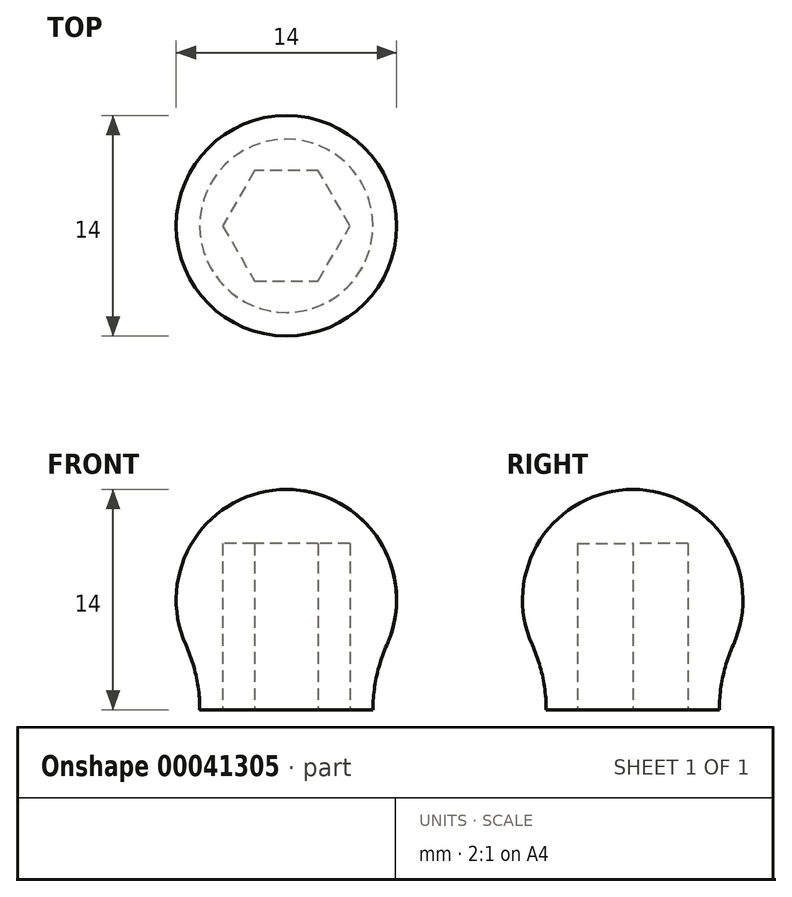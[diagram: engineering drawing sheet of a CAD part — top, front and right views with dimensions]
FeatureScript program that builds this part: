
annotation { "Feature Type Name" : "Feature", "Feature Type Description" : "" }
export const myFeature = defineFeature(function(context is Context, id is Id, definition is map)
    precondition{}
    {
        {
            var Q0;
            Q0=qCreatedBy(makeId("Front.planeOp"),FACE);
            var sketch = newSketch(context, id + "F0", { "sketchPlane" : qUnion([Q0])});
            skArc(sketch, "E0", {"start": v(0, 14) * mm, "mid": v(-6.3, 10.06) * mm, "end": v(-5.5, 2.67) * mm});
            skLineSegment(sketch, "E1", {"start": v(-5.5, 2.67) * mm, "end": v(-5.5, 0) * mm});
            skLineSegment(sketch, "E2", {"start": v(-5.5, 0) * mm, "end": v(-3.5, 0) * mm});
            skLineSegment(sketch, "E3", {"start": v(0, 0) * mm, "end": v(0, 10.57) * mm, "construction": true});
            skArc(sketch, "E4", {"start": v(-5.5, 2.67) * mm, "mid": v(-3.06, 0.7) * mm, "end": v(0, 0) * mm, "construction": true});
            skLineSegment(sketch, "E5", {"start": v(-3.5, 0) * mm, "end": v(-3.5, 10.57) * mm});
            skLineSegment(sketch, "E6", {"start": v(-3.5, 10.57) * mm, "end": v(0, 10.57) * mm});
            skLineSegment(sketch, "E7", {"start": v(-3.5, 0) * mm, "end": v(0, 0) * mm, "construction": true});
            skLineSegment(sketch, "E8", {"start": v(0, 10.57) * mm, "end": v(0, 14) * mm});
            skLineSegment(sketch, "E9", {"start": v(-4.9, 12) * mm, "end": v(-3.5, 10.57) * mm, "construction": true});
            skSolve(sketch);
        }
        {
            var Q0;
            Q0=makeQuery(id+"F0.imprint","IMPRINT",FACE,{"disambiguationData":[TD([[makeQuery(id+"F0.imprint","IMPRINT",EDGE,{"derivedFrom":sQuery(id+"F0.wireOp",EDGE,"E0")}),1.0]])]});
            var Q1;
            Q1=sQuery(id+"F0.wireOp",EDGE,"E3");
            revolve(context, id + "F1", {"entities" : qUnion([Q0]), "axis" : qUnion([Q1]), "revolveType" : RevolveType.FULL});
        }
        {
            var Q0;
            Q0=makeQuery(id+"F1.opRevolve","SWEPT_FACE",FACE,{"disambiguationData":[OSD([sQuery(id+"F0.wireOp",EDGE,"E2")])]});
            var sketch = newSketch(context, id + "F2", { "sketchPlane" : qUnion([Q0])});
            skCircle(sketch, "E10.cCircle", {"center": v(0, 0) * mm, "radius": 3.5 * mm, "construction": true});
            skLineSegment(sketch, "E10.0", {"start": v(2.02, -3.5) * mm, "end": v(-2.02, -3.5) * mm});
            skLineSegment(sketch, "E10.1", {"start": v(-2.02, -3.5) * mm, "end": v(-4.04, 0) * mm});
            skLineSegment(sketch, "E10.2", {"start": v(-4.04, 0) * mm, "end": v(-2.02, 3.5) * mm});
            skLineSegment(sketch, "E10.3", {"start": v(-2.02, 3.5) * mm, "end": v(2.02, 3.5) * mm});
            skLineSegment(sketch, "E10.4", {"start": v(2.02, 3.5) * mm, "end": v(4.04, 0) * mm});
            skLineSegment(sketch, "E10.5", {"start": v(4.04, 0) * mm, "end": v(2.02, -3.5) * mm});
            skPoint(sketch, "E10.0.midPoint", {"position": v(0, -3.5) * mm});
            skSolve(sketch);
        }
        {
            var Q0;
            {var subQ1=sQuery(id+"F2.wireOp",EDGE,"E10.1");var subQ3=sQuery(id+"F2.wireOp",EDGE,"E10.0");var subQ5=makeQuery(id+"F2.imprint","INTERSECT",VERTEX,{"derivedFrom":[subQ3,subQ1]});Q0=makeQuery(id+"F2.imprint","IMPRINT",FACE,{"disambiguationData":[TD([[makeQuery(id+"F2.imprint","IMPRINT",EDGE,{"disambiguationData":[TD([[subQ5,1.0]])],"derivedFrom":subQ3}),-1.0]])]});}
            var Q1;
            {var subQ1=sQuery(id+"F2.wireOp",EDGE,"E10.2");var subQ3=sQuery(id+"F2.wireOp",EDGE,"E10.1");var subQ5=makeQuery(id+"F2.imprint","INTERSECT",VERTEX,{"derivedFrom":[subQ3,subQ1]});Q1=makeQuery(id+"F2.imprint","IMPRINT",FACE,{"disambiguationData":[TD([[makeQuery(id+"F2.imprint","IMPRINT",EDGE,{"disambiguationData":[TD([[subQ5,1.0]])],"derivedFrom":subQ3}),-1.0]])]});}
            var Q2;
            {var subQ1=sQuery(id+"F2.wireOp",EDGE,"E10.3");var subQ3=sQuery(id+"F2.wireOp",EDGE,"E10.2");var subQ5=makeQuery(id+"F2.imprint","INTERSECT",VERTEX,{"derivedFrom":[subQ3,subQ1]});Q2=makeQuery(id+"F2.imprint","IMPRINT",FACE,{"disambiguationData":[TD([[makeQuery(id+"F2.imprint","IMPRINT",EDGE,{"disambiguationData":[TD([[subQ5,1.0]])],"derivedFrom":subQ3}),-1.0]])]});}
            var Q3;
            {var subQ1=sQuery(id+"F2.wireOp",EDGE,"E10.4");var subQ3=sQuery(id+"F2.wireOp",EDGE,"E10.3");var subQ5=makeQuery(id+"F2.imprint","INTERSECT",VERTEX,{"derivedFrom":[subQ3,subQ1]});Q3=makeQuery(id+"F2.imprint","IMPRINT",FACE,{"disambiguationData":[TD([[makeQuery(id+"F2.imprint","IMPRINT",EDGE,{"disambiguationData":[TD([[subQ5,1.0]])],"derivedFrom":subQ3}),-1.0]])]});}
            var Q4;
            {var subQ1=sQuery(id+"F2.wireOp",EDGE,"E10.5");var subQ3=sQuery(id+"F2.wireOp",EDGE,"E10.4");var subQ5=makeQuery(id+"F2.imprint","INTERSECT",VERTEX,{"derivedFrom":[subQ3,subQ1]});Q4=makeQuery(id+"F2.imprint","IMPRINT",FACE,{"disambiguationData":[TD([[makeQuery(id+"F2.imprint","IMPRINT",EDGE,{"disambiguationData":[TD([[subQ5,1.0]])],"derivedFrom":subQ3}),-1.0]])]});}
            var Q5;
            {var subQ1=sQuery(id+"F2.wireOp",EDGE,"E10.5");var subQ3=sQuery(id+"F2.wireOp",EDGE,"E10.0");var subQ5=makeQuery(id+"F2.imprint","INTERSECT",VERTEX,{"derivedFrom":[subQ3,subQ1]});Q5=makeQuery(id+"F2.imprint","IMPRINT",FACE,{"disambiguationData":[TD([[makeQuery(id+"F2.imprint","IMPRINT",EDGE,{"disambiguationData":[TD([[subQ5,-1.0]])],"derivedFrom":subQ3}),-1.0]])]});}
            var Q6;
            Q6=makeQuery(id+"F1.opRevolve","SWEPT_FACE",FACE,{"disambiguationData":[OSD([sQuery(id+"F0.wireOp",EDGE,"E6")])]});
            extrude(context, id + "F3", {"entities" : qUnion([Q0, Q1, Q2, Q3, Q4, Q5]), "operationType" : NewBodyOperationType.REMOVE, "endBound" : BoundingType.UP_TO_SURFACE, "oppositeDirection" : true, "endBoundEntityFace" : qUnion([Q6]), "depth" : 25 * mm});
        }
        {
            var Q0;
            Q0=makeQuery(id+"F1.opRevolve","SWEPT_EDGE",EDGE,{"disambiguationData":[OSD([sQuery(id+"F0.wireOp",EDGE,"E0"),sQuery(id+"F0.wireOp",EDGE,"E1")])]});
            fillet(context, id + "F4", {"entities" : qUnion([Q0]), "radius" : 10 * mm, "tangentPropagation" : true, "allowEdgeOverflow" : false});
        }
    });
